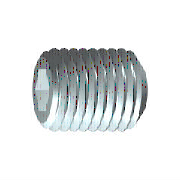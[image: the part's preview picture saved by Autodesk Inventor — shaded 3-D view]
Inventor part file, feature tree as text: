
AUTODESK INVENTOR PART (.ipt)
format: ipt  version: 2016 (Build 200138000, 138)  size: 167,936 bytes
history: native  units: mm (DEFAULTED — no unit token found)
features: sketch x2, extrude x1, other x1, plane x1
ambient origin geometry x8: Origin, YZ Plane, XZ Plane, XY Plane, X Axis, Y Axis, Z Axis, Center Point
bodies: Solid1 (feature_tree), Body (feature_tree)
feature tree (5):
  extrude  "Slot"  TaperAngle=60.0deg  [1 undecoded]
  other  "Work Axis1"
  plane  "Work Plane1"
  sketch  "Sketch1"  dims[d0=2.0mm d1=60.0deg]
  sketch  "Sketch2"  dims[d2=3.0mm d3=1.732051mm d6=90.0deg d4=0.0mm d5=4.0mm d7=0.306725mm d8=45.0deg d21=10.0mm d9=0.0mm d11=4.0mm d12=0.0mm d13=0.306725mm d14=45.0deg d15=0.0mm d29=0.306725mm d30=0.306725mm d31=0.0mm]
note: 1 required parameter value undecoded (feature->parameter linkage not recoverable at this tier; creation-order binding heuristic only, values carry confidence <= 0.55)
